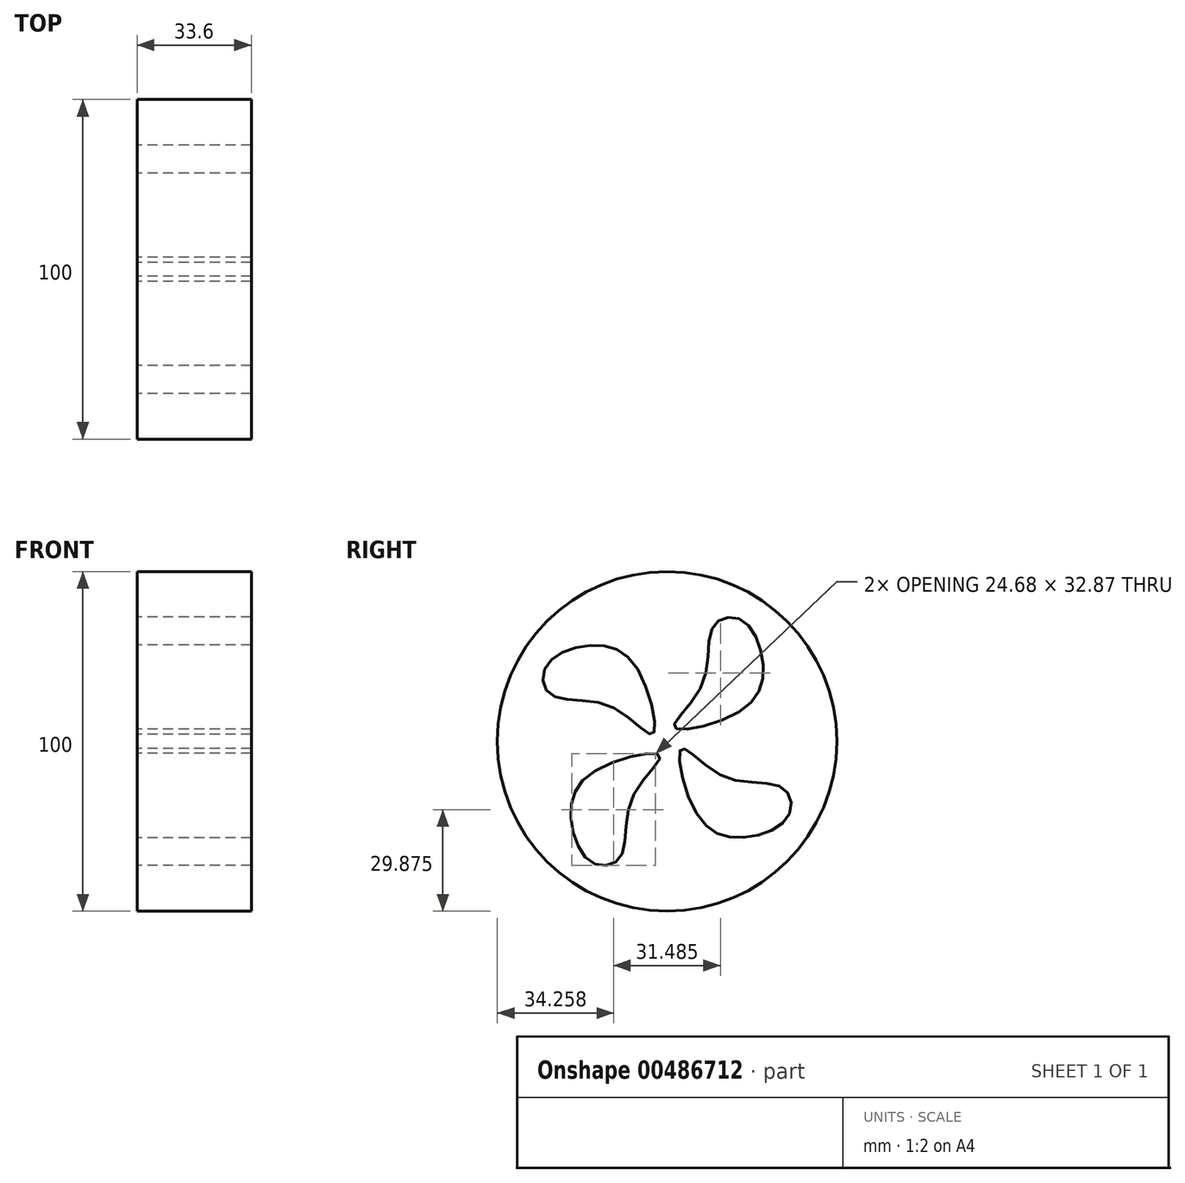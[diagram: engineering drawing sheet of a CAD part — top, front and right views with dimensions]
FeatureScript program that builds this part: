
annotation { "Feature Type Name" : "Feature", "Feature Type Description" : "" }
export const myFeature = defineFeature(function(context is Context, id is Id, definition is map)
    precondition{}
    {
        {
            var Q0;
            Q0=qCreatedBy(makeId("Right.planeOp"),FACE);
            var sketch = newSketch(context, id + "F0", { "sketchPlane" : qUnion([Q0])});
            skCircle(sketch, "E0", {"center": v(0, 0) * mm, "radius": 50 * mm});
            skSolve(sketch);
        }
        {
            var Q0;
            Q0=makeQuery(id+"F0.imprint","IMPRINT",FACE,{"disambiguationData":[TD([[makeQuery(id+"F0.imprint","IMPRINT",EDGE,{"derivedFrom":sQuery(id+"F0.wireOp",EDGE,"E0")}),1.0]])]});
            extrude(context, id + "F1", {"entities" : qUnion([Q0]), "oppositeDirection" : true, "depth" : 33.6 * mm});
        }
        {
            var Q0;
            Q0=makeQuery(id+"F1.opExtrude","CAP_FACE",FACE,{"disambiguationData":[OSD([sQuery(id+"F0.wireOp",EDGE,"E0")])],"isStart":true});
            var sketch = newSketch(context, id + "F2", { "sketchPlane" : qUnion([Q0])});
            skFitSpline(sketch, "E1", {"points": [v(21.2, 8.67) * mm, v(28.33, 21.83) * mm, v(22.16, 35.65) * mm, v(13.78, 34.21) * mm, v(10.22, 16.4) * mm, v(2.17, 4.18) * mm, v(21.2, 8.67) * mm]});
            skSolve(sketch);
        }
        {
            var Q0;
            Q0=makeQuery(id+"F2.imprint","IMPRINT",FACE,{"disambiguationData":[TD([[makeQuery(id+"F2.imprint","IMPRINT",EDGE,{"derivedFrom":sQuery(id+"F2.wireOp",EDGE,"E1")}),1.0]])]});
            extrude(context, id + "F3", {"entities" : qUnion([Q0]), "oppositeDirection" : true, "depth" : 56.8 * mm});
        }
        {
            var Q0;
            Q0=qCreatedBy(makeId("Top.planeOp"),FACE);
            var sketch = newSketch(context, id + "F4", { "sketchPlane" : qUnion([Q0])});
            skLineSegment(sketch, "E2", {"start": v(13.08, 0) * mm, "end": v(-49.61, 0) * mm, "construction": true});
            skSolve(sketch);
        }
        {
            var Q0;
            Q0=makeQuery(id+"F3.opExtrude","SWEPT_BODY",BODY,{"disambiguationData":[OSD([sQuery(id+"F2.wireOp",EDGE,"E1")])]});
            var Q1;
            Q1=sQuery(id+"F4.wireOp",EDGE,"E2");
            circularPattern(context, id + "F5", {"entities" : qUnion([Q0]), "axis" : qUnion([Q1]), "angle" : 360 * degree, "instanceCount" : 4, "equalSpace" : true});
        }
        {
            var Q0;
            Q0=makeQuery(id+"F3.opExtrude","SWEPT_BODY",BODY,{"disambiguationData":[OSD([sQuery(id+"F2.wireOp",EDGE,"E1")])]});
            var Q1;
            Q1=makeQuery(id+"F5.opPattern","COPY",BODY,{"derivedFrom":makeQuery(id+"F3.opExtrude","SWEPT_BODY",BODY,{"disambiguationData":[OSD([sQuery(id+"F2.wireOp",EDGE,"E1")])]}),"instanceName":"1"});
            var Q2;
            Q2=makeQuery(id+"F5.opPattern","COPY",BODY,{"derivedFrom":makeQuery(id+"F3.opExtrude","SWEPT_BODY",BODY,{"disambiguationData":[OSD([sQuery(id+"F2.wireOp",EDGE,"E1")])]}),"instanceName":"2"});
            var Q3;
            Q3=makeQuery(id+"F5.opPattern","COPY",BODY,{"derivedFrom":makeQuery(id+"F3.opExtrude","SWEPT_BODY",BODY,{"disambiguationData":[OSD([sQuery(id+"F2.wireOp",EDGE,"E1")])]}),"instanceName":"3"});
            var Q4;
            Q4=makeQuery(id+"F1.opExtrude","SWEPT_BODY",BODY,{"disambiguationData":[OSD([sQuery(id+"F0.wireOp",EDGE,"E0")])]});
            booleanBodies(context, id + "F6", {"operationType" : BooleanOperationType.SUBTRACTION, "tools" : qUnion([Q0, Q1, Q2, Q3]), "targets" : qUnion([Q4])});
        }
    });
